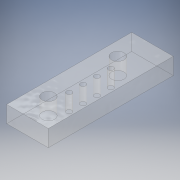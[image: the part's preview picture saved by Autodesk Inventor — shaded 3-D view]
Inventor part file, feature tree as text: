
AUTODESK INVENTOR PART (.ipt)
format: ipt  version: 2019 (Build 230136000, 136)  size: 131,072 bytes
history: native  units: mm
features: extrude x1, sketch x1
ambient origin geometry x8: Origin, YZ Plane, XZ Plane, XY Plane, X Axis, Y Axis, Z Axis, Center Point
bodies: Body1 (feature_tree)
feature tree (2):
  extrude  "Extrusion2"  Depth=15.0mm
  sketch  "Sketch2"  dims[d31=6.0mm d32=0.0mm d76=15.0mm d77=45.0mm d78=10.0mm d79=25.0mm d80=5.0mm d81=4.5mm d82=1.9mm d83=40.0mm d85=5.0mm d86=10.0mm d88=10.0mm d90=5.0mm d91=7.5mm]
